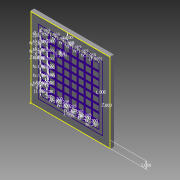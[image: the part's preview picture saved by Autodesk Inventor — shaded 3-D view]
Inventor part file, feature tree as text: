
AUTODESK INVENTOR PART (.ipt)
format: ipt  version: 2015 (Build 190159000, 159)  size: 165,888 bytes
history: native  units: in
note: dims shown in document units (in); Inventor stores cm internally (conversion verified against a paired STEP export)
features: fillet x4, sketch x2, extrude x1
ambient origin geometry x8: Origin, YZ Plane, XZ Plane, XY Plane, X Axis, Y Axis, Z Axis, Center Point
bodies: Solid1 (feature_tree)
feature tree (7):
  extrude  "Extrusion1"  Depth=22.0in
  fillet  "Fillet1"  Radius=1.0in
  fillet  "Fillet2"  Radius=0.125in
  fillet  "Fillet3"  Radius=0.125in
  fillet  "Fillet4"  Radius=0.125in
  sketch  "Sketch2"  dims[d7=0.125in d12=1.9688in d13=1.9688in d14=1.9688in d15=1.9688in d16=1.9688in d17=1.9688in d18=1.9688in d19=1.9688in d20=1.9688in d21=1.9688in d22=1.9688in d23=1.9688in d24=1.9688in d25=1.9688in d26=1.9688in d27=1.9688in d28=1.0in d29=1.0in d30=1.0in d31=1.0in d32=2.0in d33=2.0in d34=2.0in d35=2.0in d36=0.2in d37=0.2in d38=0.2in d39=0.2in d40=0.2in d41=0.2in d42=0.2in d43=0.2in d44=0.2in d45=0.2in d46=0.2in d47=0.2in d48=0.2in d49=0.2in d50=0.2in d51=0.2in d52=0.2in d53=0.2in d54=0.2in d55=0.2in d56=0.2in d57=0.2in d58=0.2in d59=0.2in d60=0.2in d61=0.2in d62=0.2in d63=1.5688in d64=1.5688in d65=0.2in]
  sketch  "Sketch1"  dims[d0=22.0in d1=22.0in d2=1.0in d3=0.0in d4=0.125in d5=0.125in d6=0.125in]
